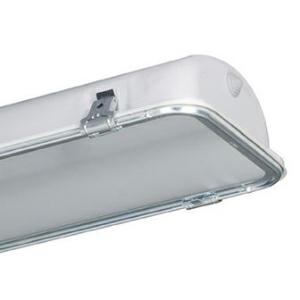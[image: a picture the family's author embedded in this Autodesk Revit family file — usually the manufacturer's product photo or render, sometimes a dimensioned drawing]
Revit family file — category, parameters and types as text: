
# Revit family: 3f_filippi_-_beta_i3f_76_vs_ampio_3f_filippi_-_55147_-_i3f_led_762x24w_ep_ampio_vs_l1265
name_source: partatom
category: Lighting Fixtures
units: mm (PartAtom-declared; Revit-internal decimal feet)

## family parameters
Cut with Voids When Loaded = No
Host = Face
Light Source = No
Part Type = Normal
Room Calculation Point = No
Round Connector Dimension = Use Diameter
Shared = No

## types (1)
- 3F Filippi - Beta i3F 76 VS Ampio (1 x LED, 6783 lm, 55 W, 4000 K)
    Apparent Load = 55 VA
    Approval mark = ENEC
    CIE Flux Codes = 62 90 98 100 100
    Color Rendering = 80
    Color Temperature = 4000 K
    Control Gear = Electronic ballast
    Default Elevation = 1800 mm
    Description = ILLUMINOTECHNICAL
Luminous efficiency 100% (DLOR 100%, ULOR 0%).
Initial luminous flux of the luminaire 6783 lm.
Emergency luminaire luminous flux BLF 7.1%.
Wide symmetric distribution.
Installation Interdistance Transv.D = 1.31 x hu - Long.D = 1.31 x hu.
Tabular UGR (CIE 117 - 4H-8H; S=0.25H; 70/50/20): RUG 19.7 - 20.9.
Beam angle: 90° - 99°.
Luminous efficacy 123 lm/W.
Lifetime (L93/B10): 30000 h. (tq+25°C)
Lifetime (L90/B10): 50000 h. (tq+25°C)
Lifetime (L85/B10): 80000 h. (tq+25°C)
Lifetime (L80/B10): 100000 h. (tq+25°C)
Sudden decreased luminous flux after 50000 hours: 0% (C0).
Photobiological safety in compliance with IEC/TR 62778: RG0 risk exempt, (IEC 62471).
In compliance with IEC/EN 62722-2-1 - IEC/EN 62717 standards.

SOURCE
2 linear LED modules 24W/840.
Energy efficiency class (UE 2019/2020 - UE 2019/2015): D.
CIE 13.3 Colour rendering index: CRI >80 (R9 <50%).
IES TM-30 Fidelity Index: Rf = 84 Rg = 95.
CCT nominal colour temperature 4000 K.
Colour initial tolerance (MacAdam): SDCM 3.

MECHANICAL
Single-piece housing in pressed steel, powder-coated in white epoxy-polyester.
Moulded anti-glare glass, non-combustible, tempered, mounted and locked to the single-piece galvanised steel perimetrical frame, sealing gasket, hinged opening by means of galvanised steel clips.
Wide flow recuperator, oversized, in specular aluminium with superficial titanium-magnesium treatment, non-iridescent.
Gear-tray unit in hot-galvanised steel, painted in white polyester, fixed to the housing by means of "Ribloc" rapid devices in galvanised steel, hinged opening.
Luminaire with limited surface temperature. - D - (EN 60598-2-24)
Dimensions: 1265x235 mm, height 105 mm. Weight 8.515 kg.
IP65 protection degree.
Mechanical strength to impacts IK09 (10 joule).
Glow-wire test resistance 960°C.

ELECTRICAL
Halogen Free electronic wiring 230V-50/60Hz, power factor 0.95, THD <25%, constant output current, SELV, class I, 1 driver.
Power of the luminaire 55 W.
CE - IEC 60598-1 - EN 60598-1.
EP maintained emergency wiring on board, 1h duration, 24h recharge; compliant with EN 60598-2-22, excluding high risk areas.
SAFE FLICKER: PstLM=<1 and SVM=<0.4 (IEC TR 61547-1 and IEC TR 63158), to ensure a more comfortable and safe light.
Ambient temperature from +5°C to +25°C.
Temperature class T6 max 85°C.
Relative humidity UR: <85%.

INSTALLATION
Ceiling / Suspended / Wall.
All accessories dedicated to this product are available on the Catalog and on our website www.3F-Filippi.com.

APPLICATIONS
In industrial environments, stores and dry, dusty indoor environments, subject to occasional water splashes.

WARNING
Fixture not suitable for cold stores with an ambient temperature <5°C and/or relative humidity >85%.
Luminaire designed for disposal/recycling at end-of-life.
Replaceable (LED only) light source by a professional. Replaceable control gear by a professional.
    Height = 105 mm
    Lamp = 1 x LED
    Lamp Light Flux = 6783 lm
    Lamp Power = 55 W
    Lamp count = 1
    Length = 1265 mm
    Lifetime = 50000 h
    Luminous efficacy = 123 lm/W
    Manufacturer = 3F Filippi
    ModVariant = No
    Model = 3F Filippi - 55147 - i3F LED 762x24W EP AMPIO VS L1265
    Mounting Place = Ceiling
    Mounting Type = Pendant
    Number of Poles = 1
    OnlyDefault = Yes
    Power Factor = 1
    Product Name = 3F Filippi - Beta i3F 76 VS Ampio
    Product group = pendant luminaire
    ProductGroupID = 9
    Protection Class = Protection class I
    Protection Degree = IP 65
    RLX_Detail_Level = 1
    RLX_Emergency_Light_Flux = 0 lm
    RLX_Emergency_Type = 0
    RLX_Emergency_Type_DB = No
    RlxData = <blob elided: 64341 chars, md5=47b66a39>
    Socket = socket
    Standby Power = 0 W
    System Light Flux = 6783 lm
    System Power = 55 W
    Type Comments = Product without accessories
    Type Image = 3ffilippi_55147.jpg
    URL = http://relux.com
    VarID = ---
    Voltage = 0 V
    Weight = 0.00 kg
    Width = 235 mm

## geometry (parser evidence)
native form markers: Blend x4, Sweep x9
no freeform markers — native parametric forms only
